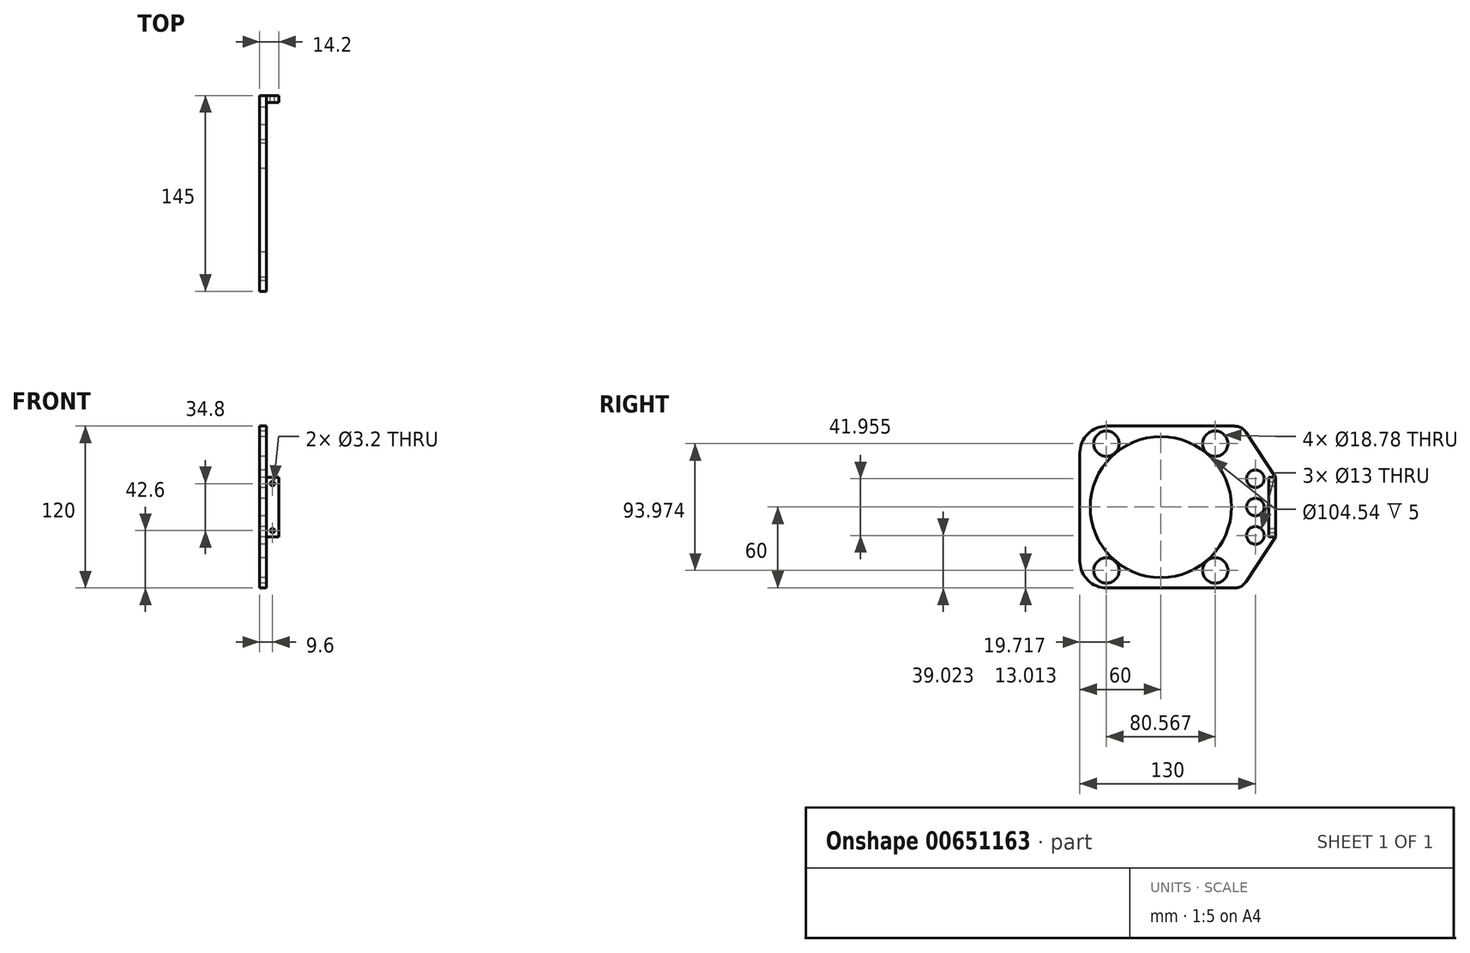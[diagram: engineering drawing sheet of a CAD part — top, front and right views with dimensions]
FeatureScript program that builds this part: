
annotation { "Feature Type Name" : "Feature", "Feature Type Description" : "" }
export const myFeature = defineFeature(function(context is Context, id is Id, definition is map)
    precondition{}
    {
        {
            var Q0;
            Q0=qCreatedBy(makeId("Front.planeOp"),FACE);
            var sketch = newSketch(context, id + "F0", { "sketchPlane" : qUnion([Q0])});
            skLineSegment(sketch, "E0.bottom", {"start": v(4.6, 22) * mm, "end": v(-4.6, 22) * mm});
            skLineSegment(sketch, "E0.top", {"start": v(4.6, -22) * mm, "end": v(-4.6, -22) * mm});
            skLineSegment(sketch, "E0.left", {"start": v(4.6, 22) * mm, "end": v(4.6, -22) * mm});
            skLineSegment(sketch, "E0.right", {"start": v(-4.6, 22) * mm, "end": v(-4.6, -22) * mm});
            skPoint(sketch, "E0.middle", {"position": v(0, 0) * mm});
            skCircle(sketch, "E1", {"center": v(0, 17.4) * mm, "radius": 1.6 * mm});
            skCircle(sketch, "E2.MirrorC", {"center": v(0, -17.4) * mm, "radius": 1.6 * mm});
            skLineSegment(sketch, "E3.bottom", {"start": v(-4.6, 22) * mm, "end": v(-9.6, 22) * mm});
            skLineSegment(sketch, "E3.top", {"start": v(-4.6, -22) * mm, "end": v(-9.6, -22) * mm});
            skLineSegment(sketch, "E3.right", {"start": v(-9.6, 22) * mm, "end": v(-9.6, -22) * mm});
            skSolve(sketch);
        }
        {
            var Q0;
            Q0=makeQuery(id+"F0.imprint","IMPRINT",FACE,{"disambiguationData":[TD([[makeQuery(id+"F0.imprint","IMPRINT",EDGE,{"derivedFrom":sQuery(id+"F0.wireOp",EDGE,"E3.bottom")}),1.0]])]});
            var Q1;
            Q1=makeQuery(id+"F0.imprint","IMPRINT",FACE,{"disambiguationData":[TD([[makeQuery(id+"F0.imprint","IMPRINT",EDGE,{"derivedFrom":sQuery(id+"F0.wireOp",EDGE,"E0.bottom")}),1.0]])]});
            extrude(context, id + "F1", {"entities" : qUnion([Q0, Q1]), "depth" : 5 * mm, "offsetDistance" : 25 * mm});
        }
        {
            var Q0;
            Q0=makeQuery(id+"F1.opExtrude","SWEPT_FACE",FACE,{"disambiguationData":[OSD([sQuery(id+"F0.wireOp",EDGE,"E3.right")])]});
            var sketch = newSketch(context, id + "F2", { "sketchPlane" : qUnion([Q0])});
            skLineSegment(sketch, "E4.bottom", {"start": v(30.4, 60) * mm, "end": v(125, 60) * mm});
            skLineSegment(sketch, "E4.top", {"start": v(30.4, -60) * mm, "end": v(125, -60) * mm});
            skLineSegment(sketch, "E4.left", {"start": v(25, 60) * mm, "end": v(25, -60) * mm, "construction": true});
            skLineSegment(sketch, "E4.right", {"start": v(145, 40) * mm, "end": v(145, -40) * mm});
            skPoint(sketch, "E4.middle", {"position": v(85, 0) * mm});
            skCircle(sketch, "E5", {"center": v(85, 0) * mm, "radius": 52.27 * mm});
            skLineSegment(sketch, "E6", {"start": v(85, 0) * mm, "end": v(85, 60) * mm, "construction": true});
            skCircle(sketch, "E7", {"center": v(44.72, 46.99) * mm, "radius": 9.39 * mm});
            skCircle(sketch, "E8.MirrorC", {"center": v(125.28, 46.99) * mm, "radius": 9.39 * mm});
            skCircle(sketch, "E9.MirrorC", {"center": v(44.72, -46.99) * mm, "radius": 9.39 * mm});
            skCircle(sketch, "E10.MirrorC", {"center": v(125.28, -46.99) * mm, "radius": 9.39 * mm});
            skLineSegment(sketch, "E11", {"start": v(22.04, 55.5) * mm, "end": v(0, 22) * mm});
            skLineSegment(sketch, "E12", {"start": v(0, -22) * mm, "end": v(22.04, -55.5) * mm});
            skCircle(sketch, "E13", {"center": v(15, 20.98) * mm, "radius": 6.5 * mm});
            skCircle(sketch, "E14", {"center": v(15, 0) * mm, "radius": 6.5 * mm});
            skCircle(sketch, "E15.MirrorC", {"center": v(15, -20.98) * mm, "radius": 6.5 * mm});
            skLineSegment(sketch, "E16", {"start": v(15, 0) * mm, "end": v(5, 0) * mm, "construction": true});
            skLineSegment(sketch, "E17", {"start": v(15, 0) * mm, "end": v(25, 0) * mm, "construction": true});
            skLineSegment(sketch, "E18", {"start": v(15, 0) * mm, "end": v(15, 20.98) * mm, "construction": true});
            skPoint(sketch, "E19.visualSharp", {"position": v(25, 60) * mm});
            skArc(sketch, "E19.filletArc", {"start": v(30.4, 60) * mm, "mid": v(25.65, 58.8) * mm, "end": v(22.04, 55.5) * mm});
            skPoint(sketch, "E20.visualSharp", {"position": v(25, -60) * mm});
            skArc(sketch, "E20.filletArc", {"start": v(22.04, -55.5) * mm, "mid": v(25.65, -58.8) * mm, "end": v(30.4, -60) * mm});
            skPoint(sketch, "E21.visualSharp", {"position": v(145, 60) * mm});
            skArc(sketch, "E21.filletArc", {"start": v(145, 40) * mm, "mid": v(139.14, 54.14) * mm, "end": v(125, 60) * mm});
            skPoint(sketch, "E22.visualSharp", {"position": v(145, -60) * mm});
            skArc(sketch, "E22.filletArc", {"start": v(125, -60) * mm, "mid": v(139.14, -54.14) * mm, "end": v(145, -40) * mm});
            skSolve(sketch);
        }
        {
            var Q0;
            Q0=makeQuery(id+"F2.imprint","IMPRINT",FACE,{"disambiguationData":[TD([[makeQuery(id+"F2.imprint","IMPRINT",EDGE,{"derivedFrom":sQuery(id+"F2.wireOp",EDGE,"E4.bottom")}),-1.0]])]});
            extrude(context, id + "F3", {"entities" : qUnion([Q0]), "operationType" : NewBodyOperationType.ADD, "oppositeDirection" : true, "depth" : 5 * mm, "offsetDistance" : 25 * mm});
        }
    });
